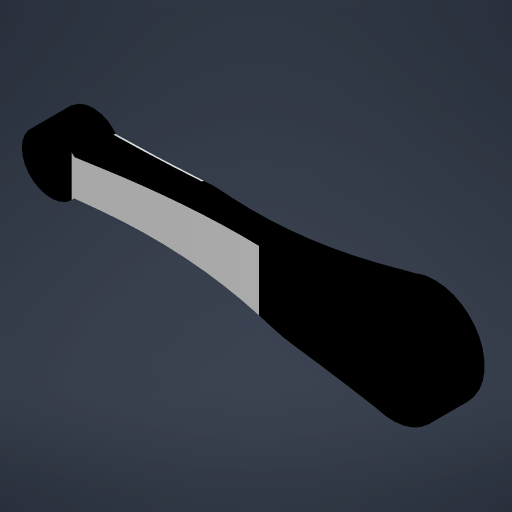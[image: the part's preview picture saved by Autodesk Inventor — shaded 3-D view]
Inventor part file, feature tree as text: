
AUTODESK INVENTOR PART (.ipt)
format: ipt  version: 2023 (Build 270158000, 158)  size: 363,520 bytes
history: native  units: mm
features: extrude x6, fillet x6, sketch x6, chamfer x4
ambient origin geometry x8: Origin, YZ Plane, XZ Plane, XY Plane, X Axis, Y Axis, Z Axis, Center Point
bodies: Solid1 (feature_tree)
feature tree (22):
  extrude  "Extrusion1"  Depth=70.0mm
  extrude  "Extrusion2"  Depth=10.0mm TaperAngle=0.0deg
  chamfer  "Chamfer1"  Distance=10.0mm Angle=45.0deg
  chamfer  "Chamfer2"  Distance=10.0mm Angle=45.0deg
  fillet  "Fillet1"  Radius=400.0mm
  fillet  "Fillet2"  Radius=100.0mm
  fillet  "Fillet3"  Radius=3.0mm
  extrude  "Extrusion3"  Depth=10.0mm
  extrude  "Extrusion4"  Depth=22.5mm
  sketch  "Sketch5"  dims[d34=22.5mm]
  chamfer  "Chamfer6"  Distance=45.0mm
  fillet  "Fillet8"  Radius=9.9mm
  extrude  "Extrusion5"  Depth=400.0mm
  extrude  "Extrusion6"  Depth=25.0mm TaperAngle=0.0deg
  fillet  "Fillet9"  Radius=50.0mm
  chamfer  "Chamfer7"  Distance=25.0mm
  fillet  "Fillet10"  Radius=2.0mm
  sketch  "Sketch1"  dims[d0=40.0mm d2=70.0mm]
  sketch  "Sketch2"  dims[d6=30.0mm d7=0.0mm d8=10.0mm d9=0.0mm d10=10.0mm d11=70.0mm d12=45.0deg d13=10.0mm d14=68.18mm d15=45.0deg d16=400.0mm d17=100.0mm d18=3.0mm]
  sketch  "Sketch3"  dims[d19=10.0mm d20=0.0mm d30=10.0mm]
  sketch  "Sketch4"  dims[d31=30.0mm d32=0.0mm d33=22.5mm]
  sketch  "Sketch6"  dims[d35=45.0mm d36=45.0mm d42=9.9mm d43=72.459481mm d44=45.0deg d46=100.0mm d47=25.0mm d48=0.0mm d49=50.0mm d50=25.0mm d51=2.0mm d52=0.0mm d53=1.0mm d55=9.9mm d56=71.769493mm d57=45.0deg d58=400.0mm d39=0.5mm d40=0.872665mm d41=0.5mm]
